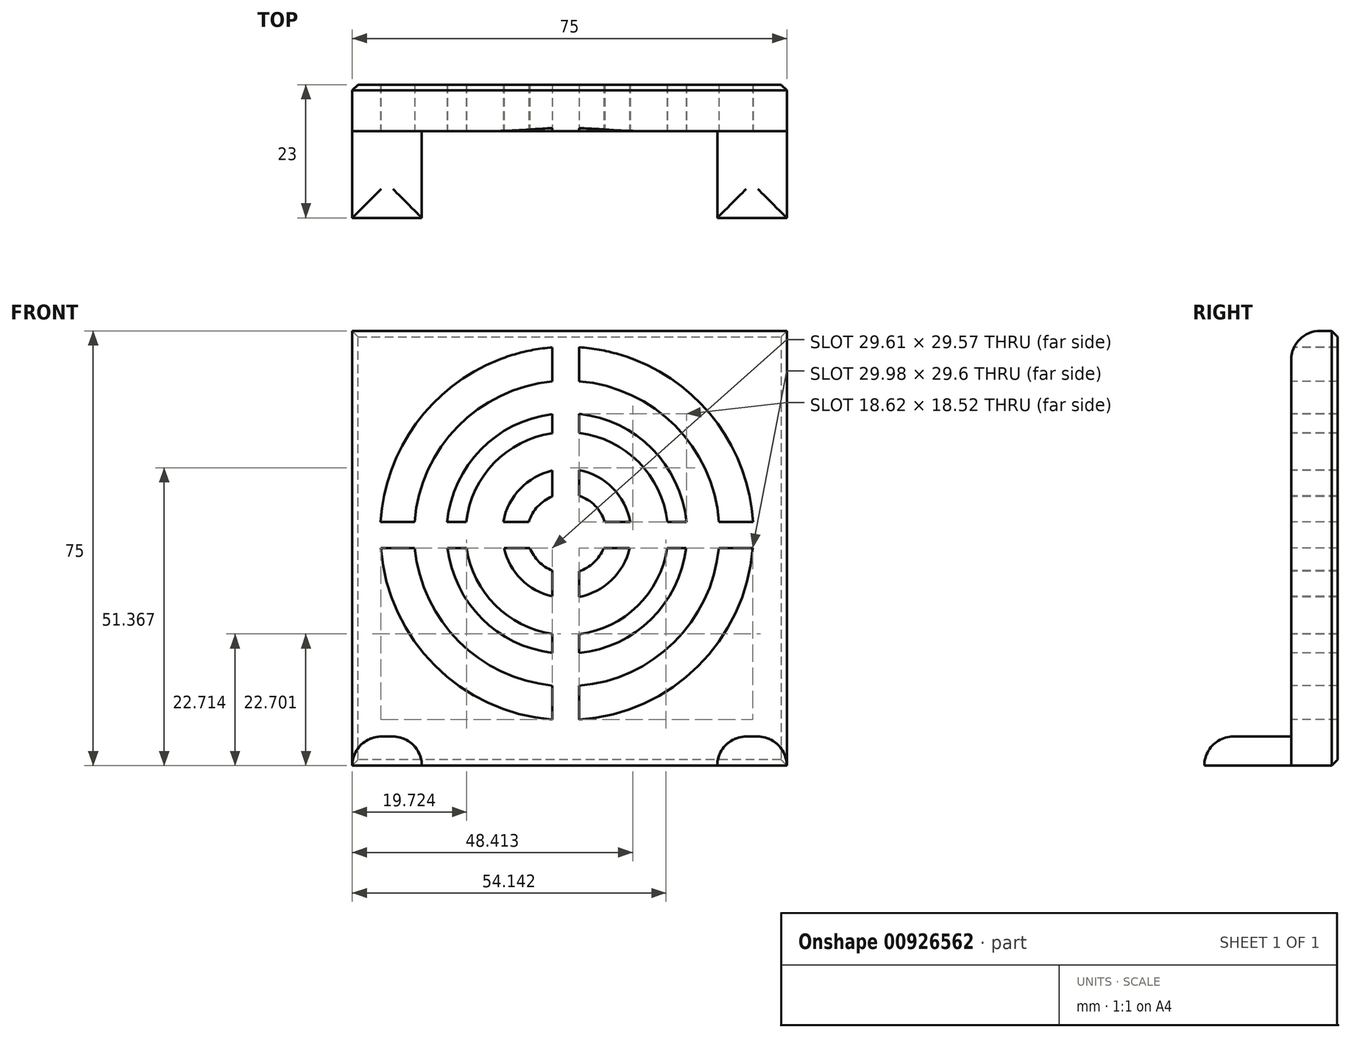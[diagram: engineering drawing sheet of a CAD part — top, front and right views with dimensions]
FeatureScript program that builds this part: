
annotation { "Feature Type Name" : "Feature", "Feature Type Description" : "" }
export const myFeature = defineFeature(function(context is Context, id is Id, definition is map)
    precondition{}
    {
        {
            var Q0;
            Q0=qCreatedBy(makeId("Front.planeOp"),FACE);
            var sketch = newSketch(context, id + "F0", { "sketchPlane" : qUnion([Q0])});
            skLineSegment(sketch, "E0.bottom", {"start": v(0, 0) * mm, "end": v(75, 0) * mm});
            skLineSegment(sketch, "E0.top", {"start": v(0, 75) * mm, "end": v(75, 75) * mm});
            skLineSegment(sketch, "E0.left", {"start": v(0, 0) * mm, "end": v(0, 75) * mm});
            skLineSegment(sketch, "E0.right", {"start": v(75, 0) * mm, "end": v(75, 75) * mm});
            skSolve(sketch);
        }
        {
            var Q0;
            Q0 = qSketchRegion(id + "F0", true);
            extrude(context, id + "F1", {"entities" : qUnion([Q0]), "depth" : 8 * mm, "offsetDistance" : 25 * mm});
        }
        {
            var Q0;
            Q0=makeQuery(id+"F1.opExtrude","CAP_FACE",FACE,{"disambiguationData":[OSD([sQuery(id+"F0.wireOp",EDGE,"E0.bottom"),sQuery(id+"F0.wireOp",EDGE,"E0.top"),sQuery(id+"F0.wireOp",EDGE,"E0.left"),sQuery(id+"F0.wireOp",EDGE,"E0.right")])],"isStart":false});
            var sketch = newSketch(context, id + "F2", { "sketchPlane" : qUnion([Q0])});
            skCircle(sketch, "E1", {"center": v(37.03, 40.04) * mm, "radius": 6.85 * mm});
            skCircle(sketch, "E2", {"center": v(37.03, 40.04) * mm, "radius": 11.15 * mm});
            skCircle(sketch, "E3", {"center": v(37.03, 40.04) * mm, "radius": 17.48 * mm});
            skCircle(sketch, "E4", {"center": v(37.03, 40.04) * mm, "radius": 20.75 * mm});
            skCircle(sketch, "E5", {"center": v(37.03, 40.04) * mm, "radius": 26.36 * mm});
            skCircle(sketch, "E6", {"center": v(37.03, 40.04) * mm, "radius": 32.2 * mm});
            skSolve(sketch);
        }
        {
            var Q0;
            Q0=makeQuery(id+"F2.imprint","IMPRINT",FACE,{"disambiguationData":[TD([[makeQuery(id+"F2.imprint","IMPRINT",EDGE,{"derivedFrom":sQuery(id+"F2.wireOp",EDGE,"E1")}),-1.0]])]});
            var Q1;
            Q1=makeQuery(id+"F2.imprint","IMPRINT",FACE,{"disambiguationData":[TD([[makeQuery(id+"F2.imprint","IMPRINT",EDGE,{"derivedFrom":sQuery(id+"F2.wireOp",EDGE,"E3")}),-1.0]])]});
            var Q2;
            Q2=makeQuery(id+"F2.imprint","IMPRINT",FACE,{"disambiguationData":[TD([[makeQuery(id+"F2.imprint","IMPRINT",EDGE,{"derivedFrom":sQuery(id+"F2.wireOp",EDGE,"E5")}),-1.0]])]});
            extrude(context, id + "F3", {"entities" : qUnion([Q0, Q1, Q2]), "operationType" : NewBodyOperationType.REMOVE, "endBound" : BoundingType.THROUGH_ALL, "oppositeDirection" : true, "depth" : 25 * mm, "offsetDistance" : 25 * mm});
        }
        {
            var Q0;
            {var subQ0=sQuery(id+"F0.wireOp",EDGE,"E0.left");var subQ1=sQuery(id+"F0.wireOp",EDGE,"E0.top");var subQ2=sQuery(id+"F0.wireOp",EDGE,"E0.right");var subQ3=sQuery(id+"F0.wireOp",EDGE,"E0.bottom");Q0=makeQuery(id+"F3.boolean.opBoolean","SPLIT",FACE,{"disambiguationData":[TD([makeQuery(id+"F1.opExtrude","SWEPT_FACE",FACE,{"disambiguationData":[OSD([subQ3])]})])],"derivedFrom":makeQuery(id+"F1.opExtrude","CAP_FACE",FACE,{"disambiguationData":[OSD([subQ3,subQ1,subQ0,subQ2])],"isStart":false})});}
            var sketch = newSketch(context, id + "F4", { "sketchPlane" : qUnion([Q0])});
            skLineSegment(sketch, "E7.bottom", {"start": v(0, 42.06) * mm, "end": v(75, 42.06) * mm});
            skLineSegment(sketch, "E7.top", {"start": v(0, 37.5) * mm, "end": v(75, 37.5) * mm});
            skLineSegment(sketch, "E7.left", {"start": v(0, 42.06) * mm, "end": v(0, 37.5) * mm});
            skLineSegment(sketch, "E7.right", {"start": v(75, 42.06) * mm, "end": v(75, 37.5) * mm});
            skLineSegment(sketch, "E8.bottom", {"start": v(34.53, 75) * mm, "end": v(39.15, 75) * mm});
            skLineSegment(sketch, "E8.top", {"start": v(34.53, 0) * mm, "end": v(39.15, 0) * mm});
            skLineSegment(sketch, "E8.left", {"start": v(34.53, 75) * mm, "end": v(34.53, 0) * mm});
            skLineSegment(sketch, "E8.right", {"start": v(39.15, 75) * mm, "end": v(39.15, 0) * mm});
            skSolve(sketch);
        }
        {
            var Q0;
            Q0 = qSketchRegion(id + "F4", true);
            var Q1;
            {var subQ0=sQuery(id+"F0.wireOp",EDGE,"E0.left");var subQ1=sQuery(id+"F0.wireOp",EDGE,"E0.top");var subQ2=sQuery(id+"F0.wireOp",EDGE,"E0.right");var subQ3=sQuery(id+"F0.wireOp",EDGE,"E0.bottom");Q1=makeQuery(id+"F3.boolean.opBoolean","SPLIT",FACE,{"disambiguationData":[TD([makeQuery(id+"F1.opExtrude","SWEPT_FACE",FACE,{"disambiguationData":[OSD([subQ3])]})])],"derivedFrom":makeQuery(id+"F1.opExtrude","CAP_FACE",FACE,{"disambiguationData":[OSD([subQ3,subQ1,subQ0,subQ2])],"isStart":true})});}
            extrude(context, id + "F5", {"entities" : qUnion([Q0]), "operationType" : NewBodyOperationType.ADD, "endBound" : BoundingType.UP_TO_SURFACE, "oppositeDirection" : true, "depth" : 25 * mm, "endBoundEntityFace" : qUnion([Q1]), "offsetDistance" : 25 * mm});
        }
        {
            var Q0;
            {var subQ0=sQuery(id+"F0.wireOp",EDGE,"E0.right");var subQ1=sQuery(id+"F0.wireOp",EDGE,"E0.left");var subQ2=sQuery(id+"F0.wireOp",EDGE,"E0.top");var subQ3=sQuery(id+"F0.wireOp",EDGE,"E0.bottom");var subQ4=makeQuery(id+"F1.opExtrude","CAP_FACE",FACE,{"disambiguationData":[OSD([subQ3,subQ2,subQ1,subQ0])],"isStart":false});Q0=makeQuery(id+"F5.boolean.opBoolean","MERGE",FACE,{"derivedFrom":[makeQuery(id+"F3.boolean.opBoolean","SPLIT",FACE,{"disambiguationData":[TD([makeQuery(id+"F1.opExtrude","SWEPT_FACE",FACE,{"disambiguationData":[OSD([subQ3])]})])],"derivedFrom":subQ4}),makeQuery(id+"F3.boolean.opBoolean","SPLIT",FACE,{"disambiguationData":[TD([makeQuery(id+"F3.opExtrude","SWEPT_FACE",FACE,{"disambiguationData":[OSD([sQuery(id+"F2.wireOp",EDGE,"E1")])]})])],"derivedFrom":subQ4}),makeQuery(id+"F3.boolean.opBoolean","SPLIT",FACE,{"disambiguationData":[TD([makeQuery(id+"F3.opExtrude","SWEPT_FACE",FACE,{"disambiguationData":[OSD([sQuery(id+"F2.wireOp",EDGE,"E2")])]})])],"derivedFrom":subQ4}),makeQuery(id+"F3.boolean.opBoolean","SPLIT",FACE,{"disambiguationData":[TD([makeQuery(id+"F3.opExtrude","SWEPT_FACE",FACE,{"disambiguationData":[OSD([sQuery(id+"F2.wireOp",EDGE,"E4")])]})])],"derivedFrom":subQ4}),makeQuery(id+"F5.opExtrude","CAP_FACE",FACE,{"disambiguationData":[OSD([sQuery(id+"F4.wireOp",EDGE,"E7.bottom"),sQuery(id+"F4.wireOp",EDGE,"E7.top"),sQuery(id+"F4.wireOp",EDGE,"E7.left"),sQuery(id+"F4.wireOp",EDGE,"E7.right"),sQuery(id+"F4.wireOp",EDGE,"E8.bottom"),sQuery(id+"F4.wireOp",EDGE,"E8.top"),sQuery(id+"F4.wireOp",EDGE,"E8.left"),sQuery(id+"F4.wireOp",EDGE,"E8.right")])],"isStart":true})]});}
            var sketch = newSketch(context, id + "F6", { "sketchPlane" : qUnion([Q0])});
            skLineSegment(sketch, "E9.bottom", {"start": v(0, 0) * mm, "end": v(12, 0) * mm});
            skLineSegment(sketch, "E9.top", {"start": v(0, 5) * mm, "end": v(12, 5) * mm});
            skLineSegment(sketch, "E9.left", {"start": v(0, 0) * mm, "end": v(0, 5) * mm});
            skLineSegment(sketch, "E9.right", {"start": v(12, 0) * mm, "end": v(12, 5) * mm});
            skLineSegment(sketch, "E10.bottom", {"start": v(75, 0) * mm, "end": v(63, 0) * mm});
            skLineSegment(sketch, "E10.top", {"start": v(75, 5) * mm, "end": v(63, 5) * mm});
            skLineSegment(sketch, "E10.left", {"start": v(75, 0) * mm, "end": v(75, 5) * mm});
            skLineSegment(sketch, "E10.right", {"start": v(63, 0) * mm, "end": v(63, 5) * mm});
            skSolve(sketch);
        }
        {
            var Q0;
            Q0 = qSketchRegion(id + "F6", true);
            extrude(context, id + "F7", {"entities" : qUnion([Q0]), "operationType" : NewBodyOperationType.ADD, "depth" : 15 * mm, "offsetDistance" : 25 * mm});
        }
        {
            var Q0;
            Q0=makeQuery(id+"F7.opExtrude","CAP_EDGE",EDGE,{"disambiguationData":[OSD([sQuery(id+"F6.wireOp",EDGE,"E9.top")])],"isStart":true});
            var Q1;
            Q1=makeQuery(id+"F7.opExtrude","SWEPT_EDGE",EDGE,{"disambiguationData":[OSD([sQuery(id+"F6.wireOp",EDGE,"E9.top"),sQuery(id+"F6.wireOp",EDGE,"E9.right")])]});
            var Q2;
            Q2=makeQuery(id+"F7.opExtrude","SWEPT_EDGE",EDGE,{"disambiguationData":[OSD([sQuery(id+"F0.wireOp",EDGE,"E0.left"),sQuery(id+"F6.wireOp",EDGE,"E9.top"),sQuery(id+"F6.wireOp",EDGE,"E9.left")])]});
            var Q3;
            Q3=makeQuery(id+"F7.opExtrude","CAP_EDGE",EDGE,{"disambiguationData":[OSD([sQuery(id+"F6.wireOp",EDGE,"E9.top")])],"isStart":false});
            var Q4;
            Q4=makeQuery(id+"F7.opExtrude","CAP_EDGE",EDGE,{"disambiguationData":[OSD([sQuery(id+"F6.wireOp",EDGE,"E10.top")])],"isStart":true});
            var Q5;
            Q5=makeQuery(id+"F7.opExtrude","SWEPT_EDGE",EDGE,{"disambiguationData":[OSD([sQuery(id+"F0.wireOp",EDGE,"E0.right"),sQuery(id+"F6.wireOp",EDGE,"E10.top"),sQuery(id+"F6.wireOp",EDGE,"E10.left")])]});
            var Q6;
            Q6=makeQuery(id+"F7.opExtrude","SWEPT_EDGE",EDGE,{"disambiguationData":[OSD([sQuery(id+"F6.wireOp",EDGE,"E10.top"),sQuery(id+"F6.wireOp",EDGE,"E10.right")])]});
            var Q7;
            Q7=makeQuery(id+"F7.opExtrude","CAP_EDGE",EDGE,{"disambiguationData":[OSD([sQuery(id+"F6.wireOp",EDGE,"E10.top")])],"isStart":false});
            var Q8;
            Q8=makeQuery(id+"F1.opExtrude","CAP_EDGE",EDGE,{"disambiguationData":[OSD([sQuery(id+"F0.wireOp",EDGE,"E0.top")])],"isStart":false});
            fillet(context, id + "F8", {"entities" : qUnion([Q0, Q1, Q2, Q3, Q4, Q5, Q6, Q7, Q8]), "radius" : 5 * mm, "tangentPropagation" : true, "allowEdgeOverflow" : false});
        }
        {
            var Q0;
            Q0=makeQuery(id+"F1.opExtrude","CAP_EDGE",EDGE,{"disambiguationData":[OSD([sQuery(id+"F0.wireOp",EDGE,"E0.right")])],"isStart":true});
            var Q1;
            Q1=makeQuery(id+"F1.opExtrude","CAP_EDGE",EDGE,{"disambiguationData":[OSD([sQuery(id+"F0.wireOp",EDGE,"E0.top")])],"isStart":true});
            var Q2;
            Q2=makeQuery(id+"F1.opExtrude","CAP_EDGE",EDGE,{"disambiguationData":[OSD([sQuery(id+"F0.wireOp",EDGE,"E0.left")])],"isStart":true});
            var Q3;
            Q3=makeQuery(id+"F1.opExtrude","CAP_EDGE",EDGE,{"disambiguationData":[OSD([sQuery(id+"F0.wireOp",EDGE,"E0.bottom")])],"isStart":true});
            chamfer(context, id + "F9", {"entities" : qUnion([Q0, Q1, Q2, Q3]), "width" : 1 * mm, "tangentPropagation" : true});
        }
    });
